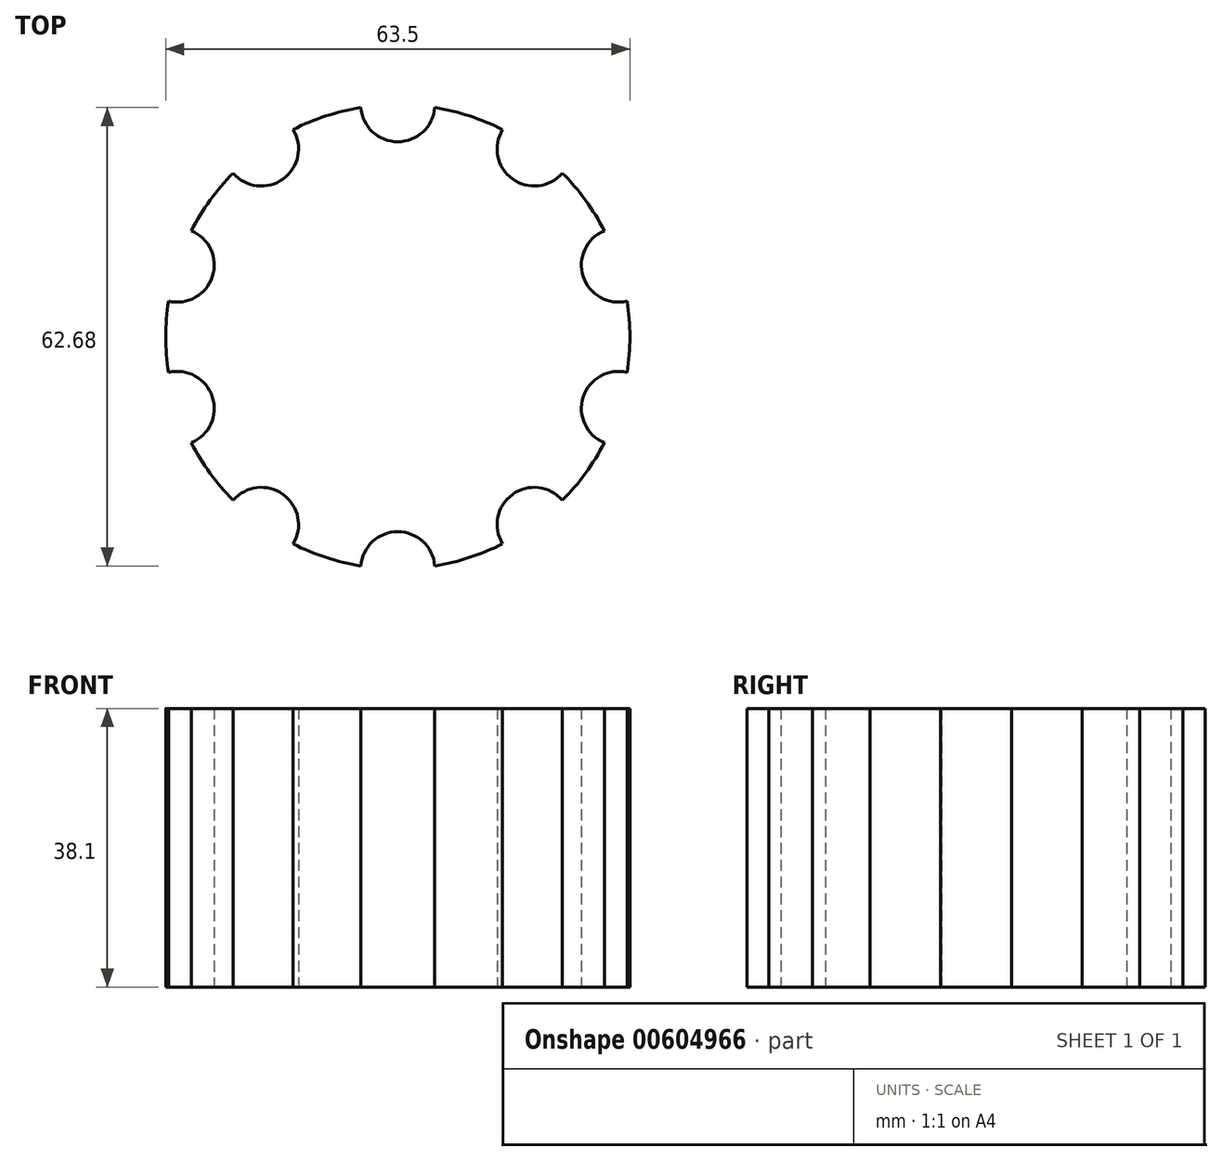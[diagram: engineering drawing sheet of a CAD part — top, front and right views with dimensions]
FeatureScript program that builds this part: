
annotation { "Feature Type Name" : "Feature", "Feature Type Description" : "" }
export const myFeature = defineFeature(function(context is Context, id is Id, definition is map)
    precondition{}
    {
        {
            var Q0;
            Q0=qCreatedBy(makeId("Top.planeOp"),FACE);
            var sketch = newSketch(context, id + "F0", { "sketchPlane" : qUnion([Q0])});
            skCircle(sketch, "E0", {"center": v(0, 0) * mm, "radius": 31.75 * mm});
            skSolve(sketch);
        }
        {
            var Q0;
            Q0=makeQuery(id+"F0.imprint","IMPRINT",FACE,{"disambiguationData":[TD([[makeQuery(id+"F0.imprint","IMPRINT",EDGE,{"derivedFrom":sQuery(id+"F0.wireOp",EDGE,"E0")}),1.0]])]});
            extrude(context, id + "F1", {"entities" : qUnion([Q0]), "depth" : 38.1 * mm});
        }
        {
            var Q0;
            Q0=qCreatedBy(makeId("Top.planeOp"),FACE);
            var sketch = newSketch(context, id + "F2", { "sketchPlane" : qUnion([Q0])});
            skCircle(sketch, "E1", {"center": v(0, 31.75) * mm, "radius": 5.08 * mm});
            skCircle(sketch, "E2.1.0", {"center": v(-18.66, 25.69) * mm, "radius": 5.08 * mm});
            skCircle(sketch, "E2.2.0", {"center": v(-30.2, 9.81) * mm, "radius": 5.08 * mm});
            skCircle(sketch, "E2.3.0", {"center": v(-30.2, -9.81) * mm, "radius": 5.08 * mm});
            skCircle(sketch, "E2.4.0", {"center": v(-18.66, -25.69) * mm, "radius": 5.08 * mm});
            skCircle(sketch, "E2.5.0", {"center": v(0, -31.75) * mm, "radius": 5.08 * mm});
            skCircle(sketch, "E2.6.0", {"center": v(18.66, -25.69) * mm, "radius": 5.08 * mm});
            skCircle(sketch, "E2.7.0", {"center": v(30.2, -9.81) * mm, "radius": 5.08 * mm});
            skCircle(sketch, "E2.8.0", {"center": v(30.2, 9.81) * mm, "radius": 5.08 * mm});
            skCircle(sketch, "E2.9.0", {"center": v(18.66, 25.69) * mm, "radius": 5.08 * mm});
            skPoint(sketch, "E2.center", {"position": v(0, 0) * mm});
            skSolve(sketch);
        }
        {
            var Q0;
            Q0=qSketchRegion(id+"F2",true);
            extrude(context, id + "F3", {"entities" : qUnion([Q0]), "depth" : 50.8 * mm});
        }
        {
            var Q0;
            Q0=makeQuery(id+"F3.opExtrude","SWEPT_BODY",BODY,{"disambiguationData":[OSD([sQuery(id+"F2.wireOp",EDGE,"E2.4.0")])]});
            var Q1;
            Q1=makeQuery(id+"F3.opExtrude","SWEPT_BODY",BODY,{"disambiguationData":[OSD([sQuery(id+"F2.wireOp",EDGE,"E2.2.0")])]});
            var Q2;
            Q2=makeQuery(id+"F3.opExtrude","SWEPT_BODY",BODY,{"disambiguationData":[OSD([sQuery(id+"F2.wireOp",EDGE,"E2.3.0")])]});
            var Q3;
            Q3=makeQuery(id+"F3.opExtrude","SWEPT_BODY",BODY,{"disambiguationData":[OSD([sQuery(id+"F2.wireOp",EDGE,"E2.5.0")])]});
            var Q4;
            Q4=makeQuery(id+"F3.opExtrude","SWEPT_BODY",BODY,{"disambiguationData":[OSD([sQuery(id+"F2.wireOp",EDGE,"E2.6.0")])]});
            var Q5;
            Q5=makeQuery(id+"F3.opExtrude","SWEPT_BODY",BODY,{"disambiguationData":[OSD([sQuery(id+"F2.wireOp",EDGE,"E2.7.0")])]});
            var Q6;
            Q6=makeQuery(id+"F3.opExtrude","SWEPT_BODY",BODY,{"disambiguationData":[OSD([sQuery(id+"F2.wireOp",EDGE,"E2.8.0")])]});
            var Q7;
            Q7=makeQuery(id+"F3.opExtrude","SWEPT_BODY",BODY,{"disambiguationData":[OSD([sQuery(id+"F2.wireOp",EDGE,"E2.9.0")])]});
            var Q8;
            Q8=makeQuery(id+"F3.opExtrude","SWEPT_BODY",BODY,{"disambiguationData":[OSD([sQuery(id+"F2.wireOp",EDGE,"E1")])]});
            var Q9;
            Q9=makeQuery(id+"F3.opExtrude","SWEPT_BODY",BODY,{"disambiguationData":[OSD([sQuery(id+"F2.wireOp",EDGE,"E2.1.0")])]});
            var Q10;
            Q10=makeQuery(id+"F1.opExtrude","SWEPT_BODY",BODY,{"disambiguationData":[OSD([sQuery(id+"F0.wireOp",EDGE,"E0")])]});
            booleanBodies(context, id + "F4", {"operationType" : BooleanOperationType.SUBTRACTION, "tools" : qUnion([Q0, Q1, Q2, Q3, Q4, Q5, Q6, Q7, Q8, Q9]), "targets" : qUnion([Q10])});
        }
    });
